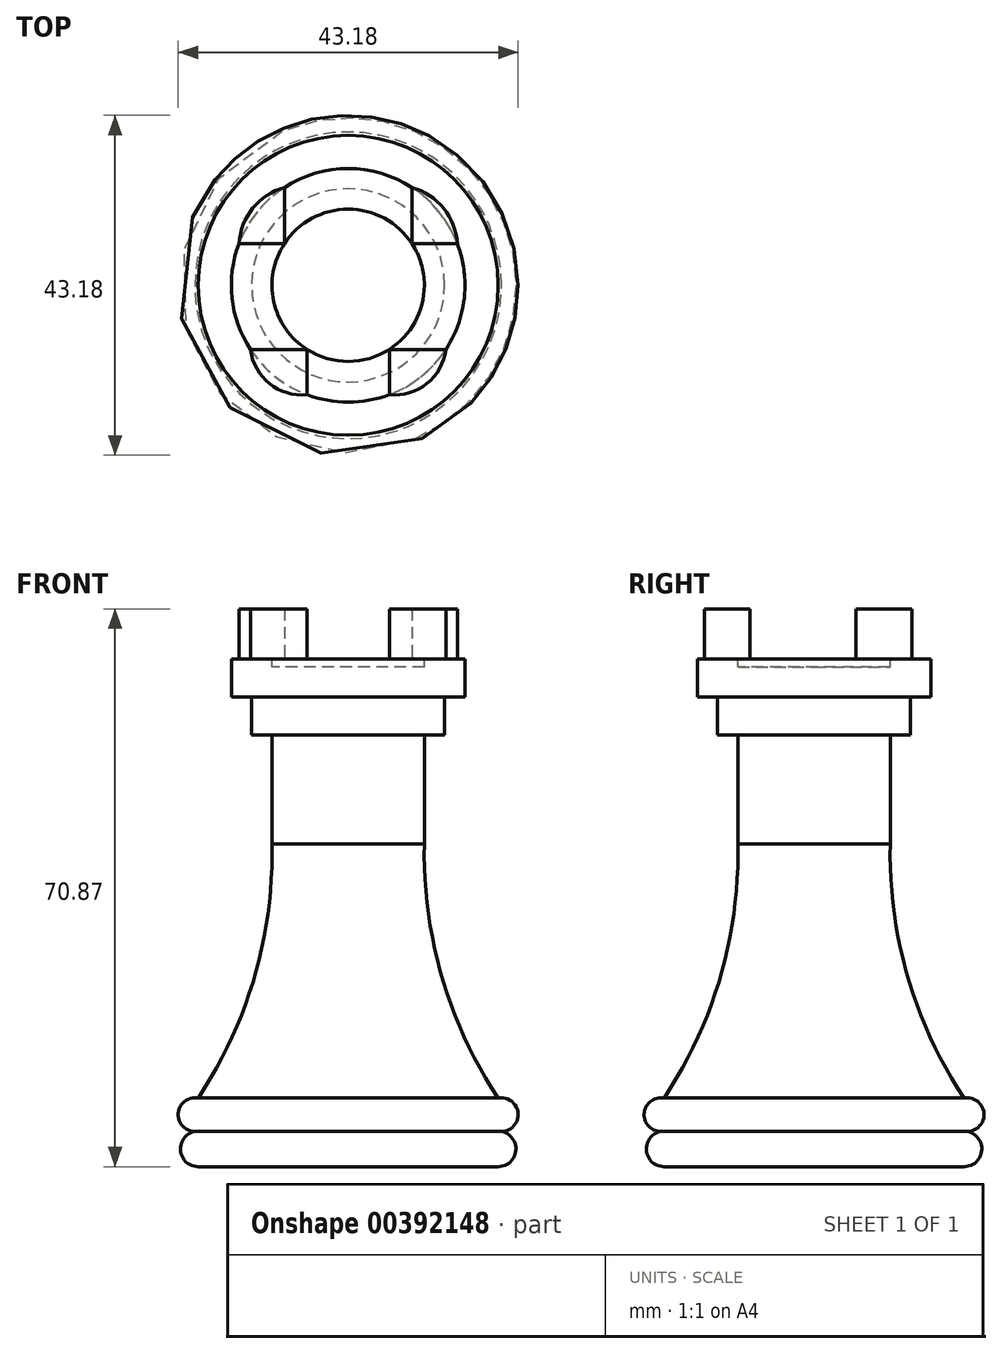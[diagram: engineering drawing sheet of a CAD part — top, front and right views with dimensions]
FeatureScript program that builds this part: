
annotation { "Feature Type Name" : "Feature", "Feature Type Description" : "" }
export const myFeature = defineFeature(function(context is Context, id is Id, definition is map)
    precondition{}
    {
        {
            var Q0;
            Q0=qCreatedBy(makeId("Front.planeOp"),FACE);
            var sketch = newSketch(context, id + "F0", { "sketchPlane" : qUnion([Q0])});
            skLineSegment(sketch, "E0", {"start": v(0, 22.53) * mm, "end": v(0, -40.97) * mm});
            skLineSegment(sketch, "E1", {"start": v(0, -40.97) * mm, "end": v(-19.05, -40.97) * mm});
            skArc(sketch, "E2", {"start": v(-19.05, -36.46) * mm, "mid": v(-21.3, -38.71) * mm, "end": v(-19.05, -40.97) * mm});
            skArc(sketch, "E3", {"start": v(-19.05, -32.26) * mm, "mid": v(-21.6, -34.36) * mm, "end": v(-19.05, -36.46) * mm});
            skArc(sketch, "E4", {"start": v(-19.05, -32.26) * mm, "mid": v(-11.9, -16.85) * mm, "end": v(-9.68, 0) * mm});
            skLineSegment(sketch, "E5", {"start": v(-9.68, 0) * mm, "end": v(-9.68, 13.87) * mm});
            skLineSegment(sketch, "E6", {"start": v(-12.26, 18.71) * mm, "end": v(-14.84, 18.71) * mm});
            skLineSegment(sketch, "E7", {"start": v(-14.84, 18.71) * mm, "end": v(-14.84, 23.55) * mm});
            skLineSegment(sketch, "E8", {"start": v(-14.84, 23.55) * mm, "end": v(-9.68, 23.55) * mm});
            skLineSegment(sketch, "E9", {"start": v(0, 23.55) * mm, "end": v(0, -40.97) * mm});
            skLineSegment(sketch, "E10.top", {"start": v(-9.68, 22.53) * mm, "end": v(0, 22.53) * mm});
            skLineSegment(sketch, "E10.left", {"start": v(-9.68, 23.55) * mm, "end": v(-9.68, 22.53) * mm});
            skLineSegment(sketch, "E10.right", {"start": v(0, 23.55) * mm, "end": v(0, 22.53) * mm});
            skLineSegment(sketch, "E11.bottom", {"start": v(-9.68, 13.87) * mm, "end": v(-12.26, 13.87) * mm});
            skLineSegment(sketch, "E11.top", {"start": v(-9.68, 18.71) * mm, "end": v(-12.26, 18.71) * mm});
            skLineSegment(sketch, "E11.right", {"start": v(-12.26, 13.87) * mm, "end": v(-12.26, 18.71) * mm});
            skPoint(sketch, "E12.orphan", {"position": v(-9.68, 18.71) * mm});
            skSolve(sketch);
        }
        {
            var Q0;
            Q0 = qSketchRegion(id + "F0", true);
            var Q1;
            Q1=sQuery(id+"F0.wireOp",EDGE,"E9");
            revolve(context, id + "F1", {"entities" : qUnion([Q0]), "axis" : qUnion([Q1]), "revolveType" : RevolveType.FULL});
        }
        {
            var Q0;
            Q0=makeQuery(id+"F1.opRevolve","SWEPT_FACE",FACE,{"disambiguationData":[OSD([sQuery(id+"F0.wireOp",EDGE,"E8")])]});
            var sketch = newSketch(context, id + "F2", { "sketchPlane" : qUnion([Q0])});
            skLineSegment(sketch, "E13", {"start": v(-13.87, 5.29) * mm, "end": v(-8.1, 5.29) * mm});
            skLineSegment(sketch, "E14", {"start": v(-8.1, 5.29) * mm, "end": v(-8.1, 12.43) * mm});
            skArc(sketch, "E15", {"start": v(-8.1, 12.43) * mm, "mid": v(-12.12, 9.78) * mm, "end": v(-13.87, 5.29) * mm});
            skLineSegment(sketch, "E16", {"start": v(0, 27.42) * mm, "end": v(0, -30.33) * mm});
            skArc(sketch, "E17.MirrorCS", {"start": v(8.1, 12.43) * mm, "mid": v(12.12, 9.78) * mm, "end": v(13.87, 5.29) * mm});
            skLineSegment(sketch, "E18.MirrorCS", {"start": v(8.1, 5.29) * mm, "end": v(8.1, 12.43) * mm});
            skLineSegment(sketch, "E19.MirrorCS", {"start": v(13.87, 5.29) * mm, "end": v(8.1, 5.29) * mm});
            skLineSegment(sketch, "E20", {"start": v(-12.4, -8.15) * mm, "end": v(-5.22, -8.15) * mm});
            skLineSegment(sketch, "E21", {"start": v(-5.22, -8.15) * mm, "end": v(-5.22, -13.9) * mm});
            skArc(sketch, "E22", {"start": v(-12.4, -8.15) * mm, "mid": v(-9.99, -12.48) * mm, "end": v(-5.22, -13.9) * mm});
            skLineSegment(sketch, "E23.MirrorCS", {"start": v(12.4, -8.15) * mm, "end": v(5.22, -8.15) * mm});
            skLineSegment(sketch, "E24.MirrorCS", {"start": v(5.22, -8.15) * mm, "end": v(5.22, -13.9) * mm});
            skArc(sketch, "E25.MirrorCS", {"start": v(12.4, -8.15) * mm, "mid": v(9.99, -12.48) * mm, "end": v(5.22, -13.9) * mm});
            skPoint(sketch, "E26.MirrorCS.end.orphan", {"position": v(-5.22, -2.4) * mm});
            skPoint(sketch, "E26.MirrorCS.start.orphan", {"position": v(-5.22, -8.15) * mm});
            skSolve(sketch);
        }
        {
            var Q0;
            Q0 = qSketchRegion(id + "F2", true);
            extrude(context, id + "F3", {"entities" : qUnion([Q0]), "operationType" : NewBodyOperationType.ADD, "depth" : 6.35 * mm});
        }
    });
